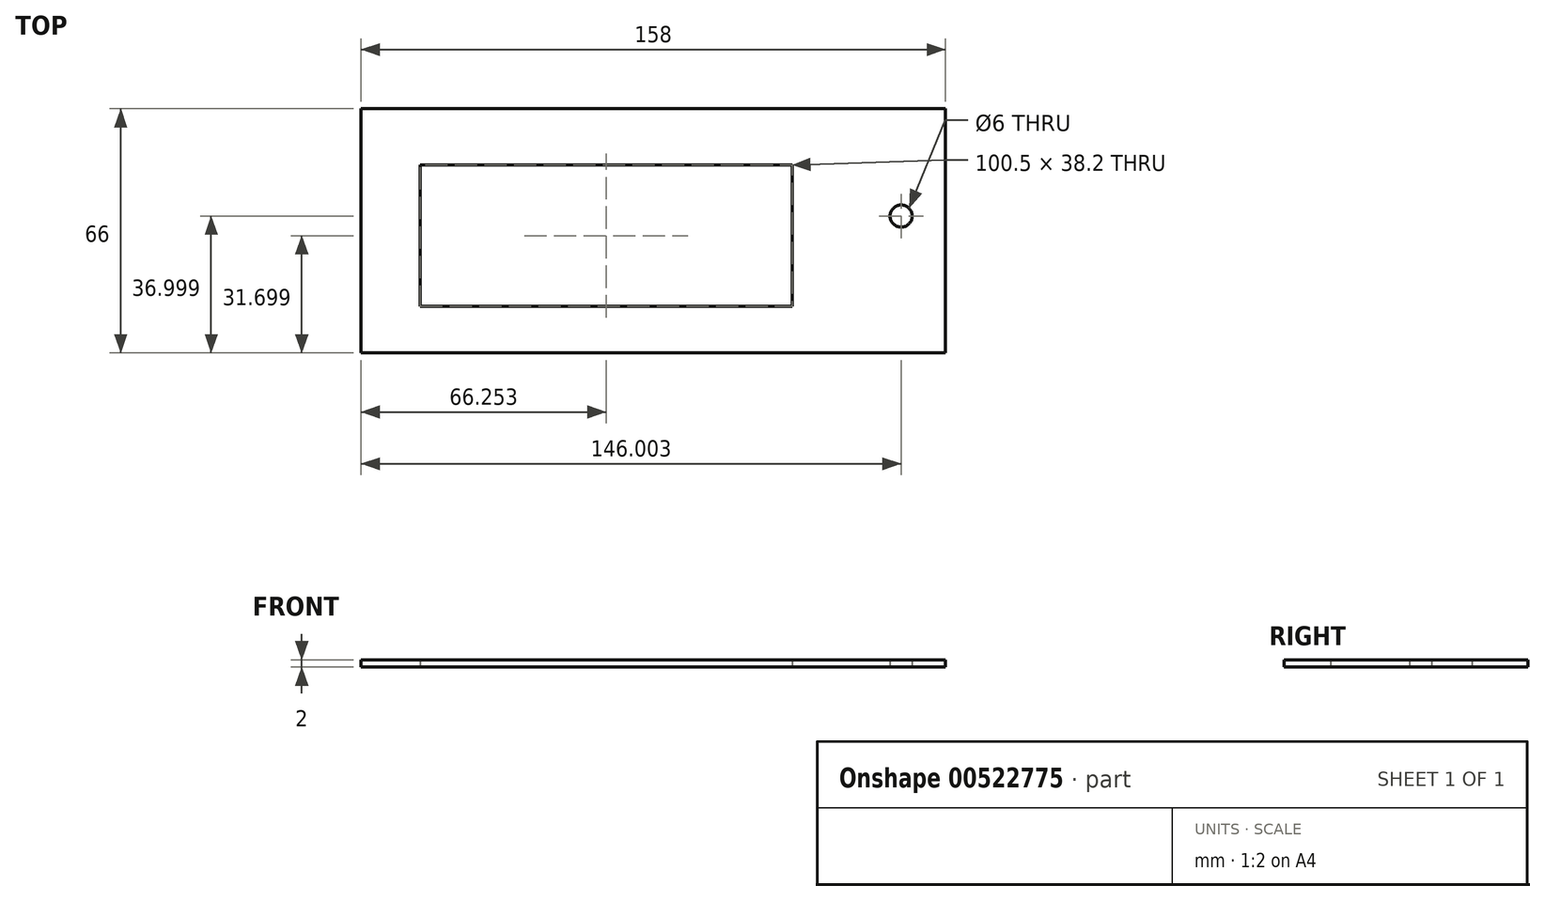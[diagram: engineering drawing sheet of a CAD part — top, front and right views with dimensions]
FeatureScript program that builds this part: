
annotation { "Feature Type Name" : "Feature", "Feature Type Description" : "" }
export const myFeature = defineFeature(function(context is Context, id is Id, definition is map)
    precondition{}
    {
        {
            var Q0;
            Q0=qCreatedBy(makeId("Top.planeOp"),FACE);
            var sketch = newSketch(context, id + "F0", { "sketchPlane" : qUnion([Q0])});
            skLineSegment(sketch, "E0.bottom", {"start": v(-82.44, 55.45) * mm, "end": v(75.56, 55.45) * mm});
            skLineSegment(sketch, "E0.top", {"start": v(-82.44, -10.55) * mm, "end": v(75.56, -10.55) * mm});
            skLineSegment(sketch, "E0.left", {"start": v(-82.44, 55.45) * mm, "end": v(-82.44, -10.55) * mm});
            skLineSegment(sketch, "E0.right", {"start": v(75.56, 55.45) * mm, "end": v(75.56, -10.55) * mm});
            skLineSegment(sketch, "E1.bottom", {"start": v(-10.04, -44.35) * mm, "end": v(17.51, -44.35) * mm});
            skLineSegment(sketch, "E1.top", {"start": v(-10.04, -56.07) * mm, "end": v(17.51, -56.07) * mm});
            skLineSegment(sketch, "E1.left", {"start": v(-10.04, -44.35) * mm, "end": v(-10.04, -56.07) * mm});
            skLineSegment(sketch, "E1.right", {"start": v(17.51, -44.35) * mm, "end": v(17.51, -56.07) * mm});
            skLineSegment(sketch, "E2.bottom", {"start": v(-66.44, 40.25) * mm, "end": v(34.06, 40.25) * mm});
            skLineSegment(sketch, "E2.top", {"start": v(-66.44, 2.05) * mm, "end": v(34.06, 2.05) * mm});
            skLineSegment(sketch, "E2.left", {"start": v(-66.44, 40.25) * mm, "end": v(-66.44, 2.05) * mm});
            skLineSegment(sketch, "E2.right", {"start": v(34.06, 40.25) * mm, "end": v(34.06, 2.05) * mm});
            skCircle(sketch, "E3", {"center": v(63.56, 26.45) * mm, "radius": 3 * mm});
            skSolve(sketch);
        }
        {
            var Q0;
            Q0=makeQuery(id+"F0.imprint","IMPRINT",FACE,{"disambiguationData":[TD([[makeQuery(id+"F0.imprint","IMPRINT",EDGE,{"derivedFrom":sQuery(id+"F0.wireOp",EDGE,"E0.bottom")}),-1.0]])]});
            extrude(context, id + "F1", {"entities" : qUnion([Q0]), "depth" : 2 * mm, "offsetDistance" : 25 * mm});
        }
    });
